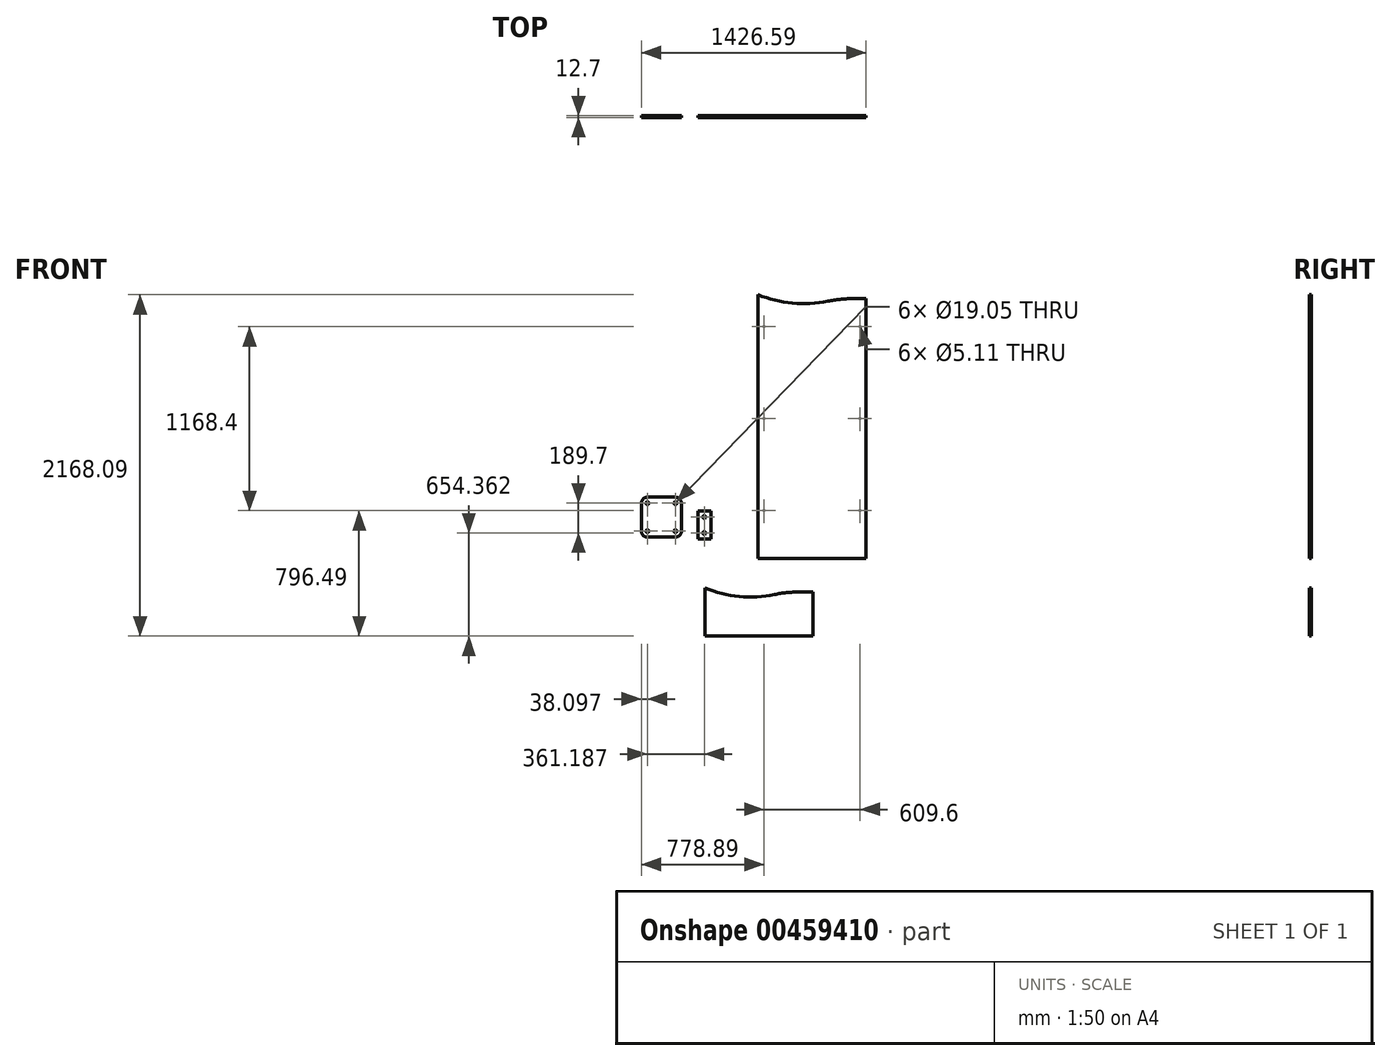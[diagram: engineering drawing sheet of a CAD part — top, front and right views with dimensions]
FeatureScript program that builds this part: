
annotation { "Feature Type Name" : "Feature", "Feature Type Description" : "" }
export const myFeature = defineFeature(function(context is Context, id is Id, definition is map)
    precondition{}
    {
        {
            var Q0;
            Q0=qCreatedBy(makeId("Front.planeOp"),FACE);
            var sketch = newSketch(context, id + "F0", { "sketchPlane" : qUnion([Q0])});
            skLineSegment(sketch, "E0.bottom", {"start": v(0, 0) * mm, "end": v(685.8, 0) * mm});
            skLineSegment(sketch, "E0.top", {"start": v(596.9, 1651) * mm, "end": v(685.8, 1651) * mm});
            skLineSegment(sketch, "E0.left", {"start": v(0, 0) * mm, "end": v(0, 1651) * mm});
            skLineSegment(sketch, "E0.right", {"start": v(685.8, 0) * mm, "end": v(685.8, 1651) * mm});
            skArc(sketch, "E1", {"start": v(596.9, 1651) * mm, "mid": v(519.48, 1647.06) * mm, "end": v(442.87, 1635.27) * mm});
            skLineSegment(sketch, "E2", {"start": v(0, 1651) * mm, "end": v(0, 1676.4) * mm});
            skArc(sketch, "E3", {"start": v(0, 1676.4) * mm, "mid": v(218.37, 1622.8) * mm, "end": v(442.87, 1635.27) * mm});
            skSolve(sketch);
        }
        {
            var Q0;
            Q0=makeQuery(id+"F0.imprint","IMPRINT",FACE,{"disambiguationData":[TD([[makeQuery(id+"F0.imprint","IMPRINT",EDGE,{"derivedFrom":sQuery(id+"F0.wireOp",EDGE,"E0.bottom")}),1.0]])]});
            extrude(context, id + "F1", {"entities" : qUnion([Q0]), "depth" : 12.7 * mm, "offsetDistance" : 25.4 * mm});
        }
        {
            var Q0;
            Q0=qCreatedBy(makeId("Front.planeOp"),FACE);
            var sketch = newSketch(context, id + "F2", { "sketchPlane" : qUnion([Q0])});
            skLineSegment(sketch, "E4", {"start": v(-41.8, 304.8) * mm, "end": v(725.2, 304.8) * mm, "construction": true});
            skLineSegment(sketch, "E5", {"start": v(-49.61, 889) * mm, "end": v(740.81, 889) * mm, "construction": true});
            skLineSegment(sketch, "E6", {"start": v(-63.27, 1473.2) * mm, "end": v(725.2, 1473.2) * mm, "construction": true});
            skLineSegment(sketch, "E7", {"start": v(38.1, 1691.1) * mm, "end": v(38.1, -26.84) * mm, "construction": true});
            skLineSegment(sketch, "E8", {"start": v(647.7, 1689.16) * mm, "end": v(647.7, -30.72) * mm, "construction": true});
            skCircle(sketch, "E9", {"center": v(38.1, 1473.2) * mm, "radius": 2.55 * mm});
            skCircle(sketch, "E10", {"center": v(38.1, 889) * mm, "radius": 2.55 * mm});
            skCircle(sketch, "E11", {"center": v(38.1, 304.8) * mm, "radius": 2.55 * mm});
            skCircle(sketch, "E12", {"center": v(647.7, 1473.2) * mm, "radius": 2.55 * mm});
            skCircle(sketch, "E13", {"center": v(647.7, 889) * mm, "radius": 2.55 * mm});
            skCircle(sketch, "E14", {"center": v(647.7, 304.8) * mm, "radius": 2.55 * mm});
            skSolve(sketch);
        }
        {
            var Q0;
            Q0 = qSketchRegion(id + "F2", true);
            extrude(context, id + "F3", {"entities" : qUnion([Q0]), "operationType" : NewBodyOperationType.REMOVE, "endBound" : BoundingType.THROUGH_ALL, "depth" : 25.4 * mm, "offsetDistance" : 25.4 * mm});
        }
        {
            var Q0;
            Q0=qCreatedBy(makeId("Front.planeOp"),FACE);
            var sketch = newSketch(context, id + "F4", { "sketchPlane" : qUnion([Q0])});
            skLineSegment(sketch, "E15.bottom", {"start": v(-740.8, 390.47) * mm, "end": v(-486.8, 390.47) * mm});
            skLineSegment(sketch, "E15.top", {"start": v(-740.8, 136.47) * mm, "end": v(-486.8, 136.47) * mm});
            skLineSegment(sketch, "E15.left", {"start": v(-740.8, 390.47) * mm, "end": v(-740.8, 136.47) * mm});
            skLineSegment(sketch, "E15.right", {"start": v(-486.8, 390.47) * mm, "end": v(-486.8, 136.47) * mm});
            skCircle(sketch, "E16", {"center": v(-702.7, 352.37) * mm, "radius": 9.53 * mm});
            skCircle(sketch, "E17.0.1.0", {"center": v(-702.7, 174.57) * mm, "radius": 9.53 * mm});
            skCircle(sketch, "E17.1.0.0", {"center": v(-524.9, 352.37) * mm, "radius": 9.53 * mm});
            skCircle(sketch, "E17.1.1.0", {"center": v(-524.9, 174.57) * mm, "radius": 9.53 * mm});
            skLineSegment(sketch, "E17.direction1", {"start": v(-702.7, 352.37) * mm, "end": v(-524.9, 352.37) * mm, "construction": true});
            skLineSegment(sketch, "E17.direction2", {"start": v(-702.7, 352.37) * mm, "end": v(-702.7, 174.57) * mm, "construction": true});
            skSolve(sketch);
        }
        {
            var Q0;
            Q0=makeQuery(id+"F4.imprint","IMPRINT",FACE,{"disambiguationData":[TD([[makeQuery(id+"F4.imprint","IMPRINT",EDGE,{"derivedFrom":sQuery(id+"F4.wireOp",EDGE,"E15.bottom")}),-1.0]])]});
            extrude(context, id + "F5", {"entities" : qUnion([Q0]), "depth" : 12.7 * mm, "offsetDistance" : 25.4 * mm});
        }
        {
            var Q0;
            Q0=makeQuery(id+"F5.opExtrude","SWEPT_EDGE",EDGE,{"disambiguationData":[OSD([sQuery(id+"F4.wireOp",EDGE,"E15.bottom"),sQuery(id+"F4.wireOp",EDGE,"E15.right")])]});
            var Q1;
            Q1=makeQuery(id+"F5.opExtrude","SWEPT_EDGE",EDGE,{"disambiguationData":[OSD([sQuery(id+"F4.wireOp",EDGE,"E15.bottom"),sQuery(id+"F4.wireOp",EDGE,"E15.left")])]});
            var Q2;
            Q2=makeQuery(id+"F5.opExtrude","SWEPT_EDGE",EDGE,{"disambiguationData":[OSD([sQuery(id+"F4.wireOp",EDGE,"E15.top"),sQuery(id+"F4.wireOp",EDGE,"E15.right")])]});
            var Q3;
            Q3=makeQuery(id+"F5.opExtrude","SWEPT_EDGE",EDGE,{"disambiguationData":[OSD([sQuery(id+"F4.wireOp",EDGE,"E15.top"),sQuery(id+"F4.wireOp",EDGE,"E15.left")])]});
            fillet(context, id + "F6", {"entities" : qUnion([Q0, Q1, Q2, Q3]), "radius" : 38.1 * mm, "tangentPropagation" : true, "allowEdgeOverflow" : false});
        }
        {
            var Q0;
            Q0=qCreatedBy(makeId("Front.planeOp"),FACE);
            var sketch = newSketch(context, id + "F7", { "sketchPlane" : qUnion([Q0])});
            skLineSegment(sketch, "E18.bottom", {"start": v(-382.78, 302.37) * mm, "end": v(-300.23, 302.37) * mm});
            skLineSegment(sketch, "E18.top", {"start": v(-382.78, 124.57) * mm, "end": v(-300.23, 124.57) * mm});
            skLineSegment(sketch, "E18.left", {"start": v(-382.78, 302.37) * mm, "end": v(-382.78, 124.57) * mm});
            skLineSegment(sketch, "E18.right", {"start": v(-300.23, 302.37) * mm, "end": v(-300.23, 124.57) * mm});
            skSolve(sketch);
        }
        {
            var Q0;
            Q0 = qSketchRegion(id + "F7", true);
            extrude(context, id + "F8", {"entities" : qUnion([Q0]), "depth" : 12.7 * mm, "offsetDistance" : 25.4 * mm});
        }
        {
            var Q0;
            Q0=makeQuery(id+"F8.opExtrude","CAP_FACE",FACE,{"disambiguationData":[OSD([sQuery(id+"F7.wireOp",EDGE,"E18.bottom"),sQuery(id+"F7.wireOp",EDGE,"E18.top"),sQuery(id+"F7.wireOp",EDGE,"E18.left"),sQuery(id+"F7.wireOp",EDGE,"E18.right")])],"isStart":false});
            var sketch = newSketch(context, id + "F9", { "sketchPlane" : qUnion([Q0])});
            skLineSegment(sketch, "E19", {"start": v(-341.5, 315.69) * mm, "end": v(-341.5, 86.09) * mm, "construction": true});
            skLineSegment(sketch, "E20", {"start": v(-397.83, 264.27) * mm, "end": v(-280.42, 264.27) * mm, "construction": true});
            skLineSegment(sketch, "E21", {"start": v(-398.87, 162.67) * mm, "end": v(-275.73, 162.67) * mm, "construction": true});
            skCircle(sketch, "E22", {"center": v(-341.5, 264.27) * mm, "radius": 9.53 * mm});
            skCircle(sketch, "E23", {"center": v(-341.5, 162.67) * mm, "radius": 9.53 * mm});
            skSolve(sketch);
        }
        {
            var Q0;
            Q0 = qSketchRegion(id + "F9", true);
            extrude(context, id + "F10", {"entities" : qUnion([Q0]), "operationType" : NewBodyOperationType.REMOVE, "endBound" : BoundingType.THROUGH_ALL, "oppositeDirection" : true, "depth" : 25.4 * mm, "offsetDistance" : 25.4 * mm});
        }
        {
            var Q0;
            Q0=qCreatedBy(makeId("Front.planeOp"),FACE);
            var sketch = newSketch(context, id + "F11", { "sketchPlane" : qUnion([Q0])});
            skLineSegment(sketch, "E24.top", {"start": v(-337.65, -491.7) * mm, "end": v(348.15, -491.7) * mm});
            skLineSegment(sketch, "E24.left", {"start": v(-337.65, -186.9) * mm, "end": v(-337.65, -491.7) * mm});
            skLineSegment(sketch, "E24.right", {"start": v(348.15, -212.3) * mm, "end": v(348.15, -491.7) * mm});
            skArc(sketch, "E25", {"start": v(-337.65, -186.9) * mm, "mid": v(-119.28, -240.49) * mm, "end": v(105.22, -228.02) * mm});
            skArc(sketch, "E26", {"start": v(259.25, -212.3) * mm, "mid": v(181.83, -216.24) * mm, "end": v(105.22, -228.02) * mm});
            skLineSegment(sketch, "E27", {"start": v(259.25, -212.3) * mm, "end": v(348.15, -212.3) * mm});
            skSolve(sketch);
        }
        {
            var Q0;
            Q0 = qSketchRegion(id + "F11", true);
            extrude(context, id + "F12", {"entities" : qUnion([Q0]), "depth" : 12.7 * mm, "offsetDistance" : 25.4 * mm});
        }
    });
